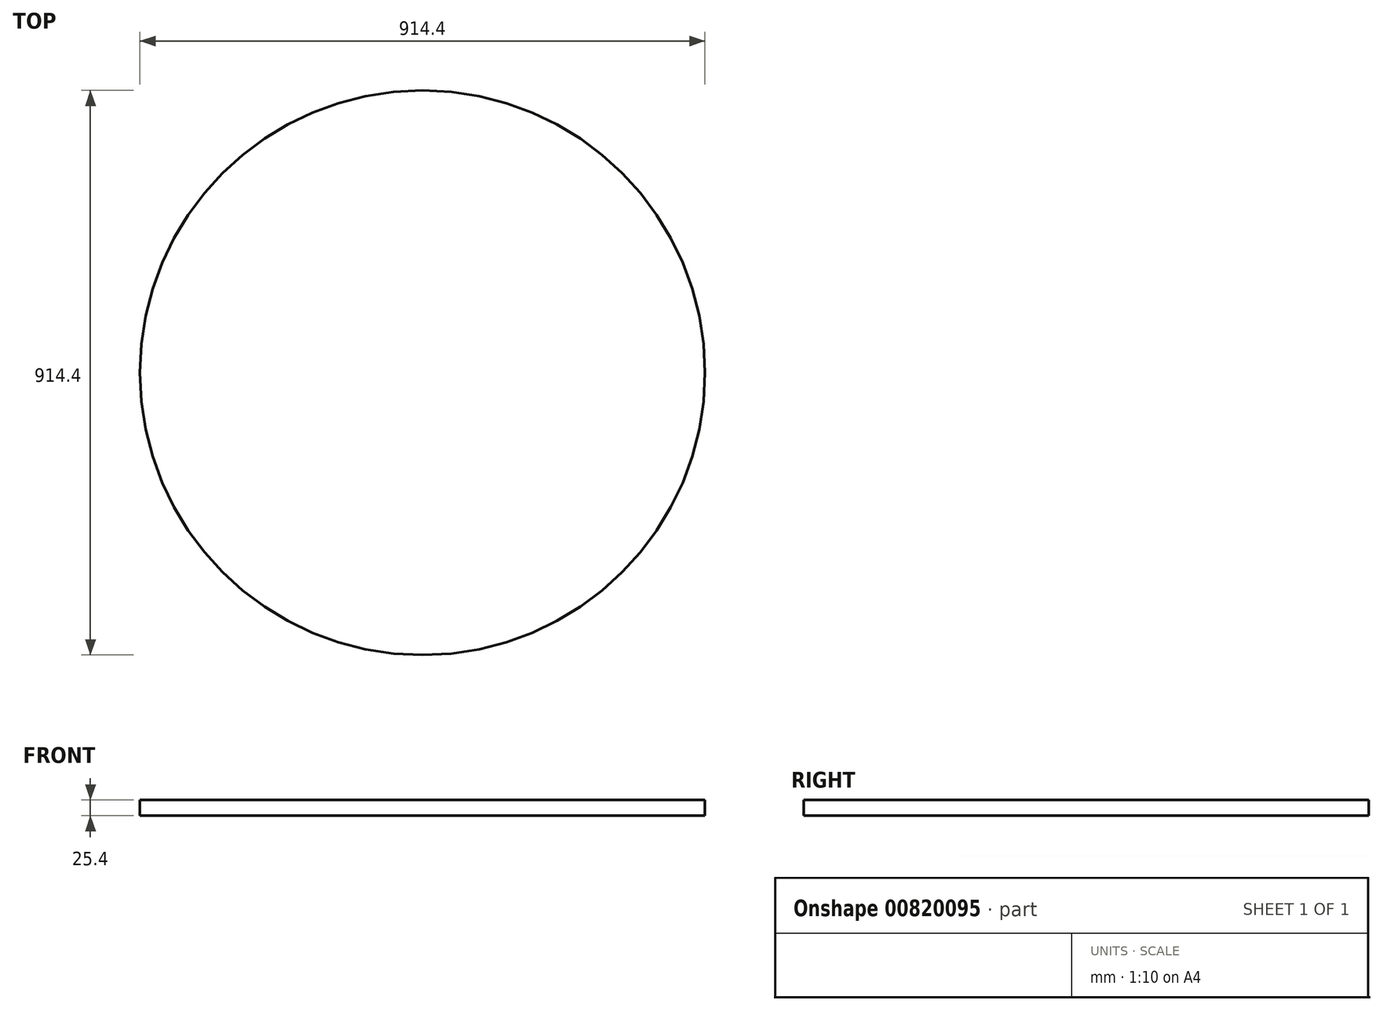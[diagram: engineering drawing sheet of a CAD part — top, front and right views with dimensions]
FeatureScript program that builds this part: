
annotation { "Feature Type Name" : "Feature", "Feature Type Description" : "" }
export const myFeature = defineFeature(function(context is Context, id is Id, definition is map)
    precondition{}
    {
        {
            var Q0;
            Q0=qCreatedBy(makeId("Top.planeOp"),FACE);
            var sketch = newSketch(context, id + "F0", { "sketchPlane" : qUnion([Q0])});
            skCircle(sketch, "E0", {"center": v(0, 0) * mm, "radius": 457.2 * mm});
            skSolve(sketch);
        }
        {
            var Q0;
            Q0 = qSketchRegion(id + "F0", true);
            extrude(context, id + "F1", {"entities" : qUnion([Q0]), "depth" : 25.4 * mm, "offsetDistance" : 25.4 * mm});
        }
    });
